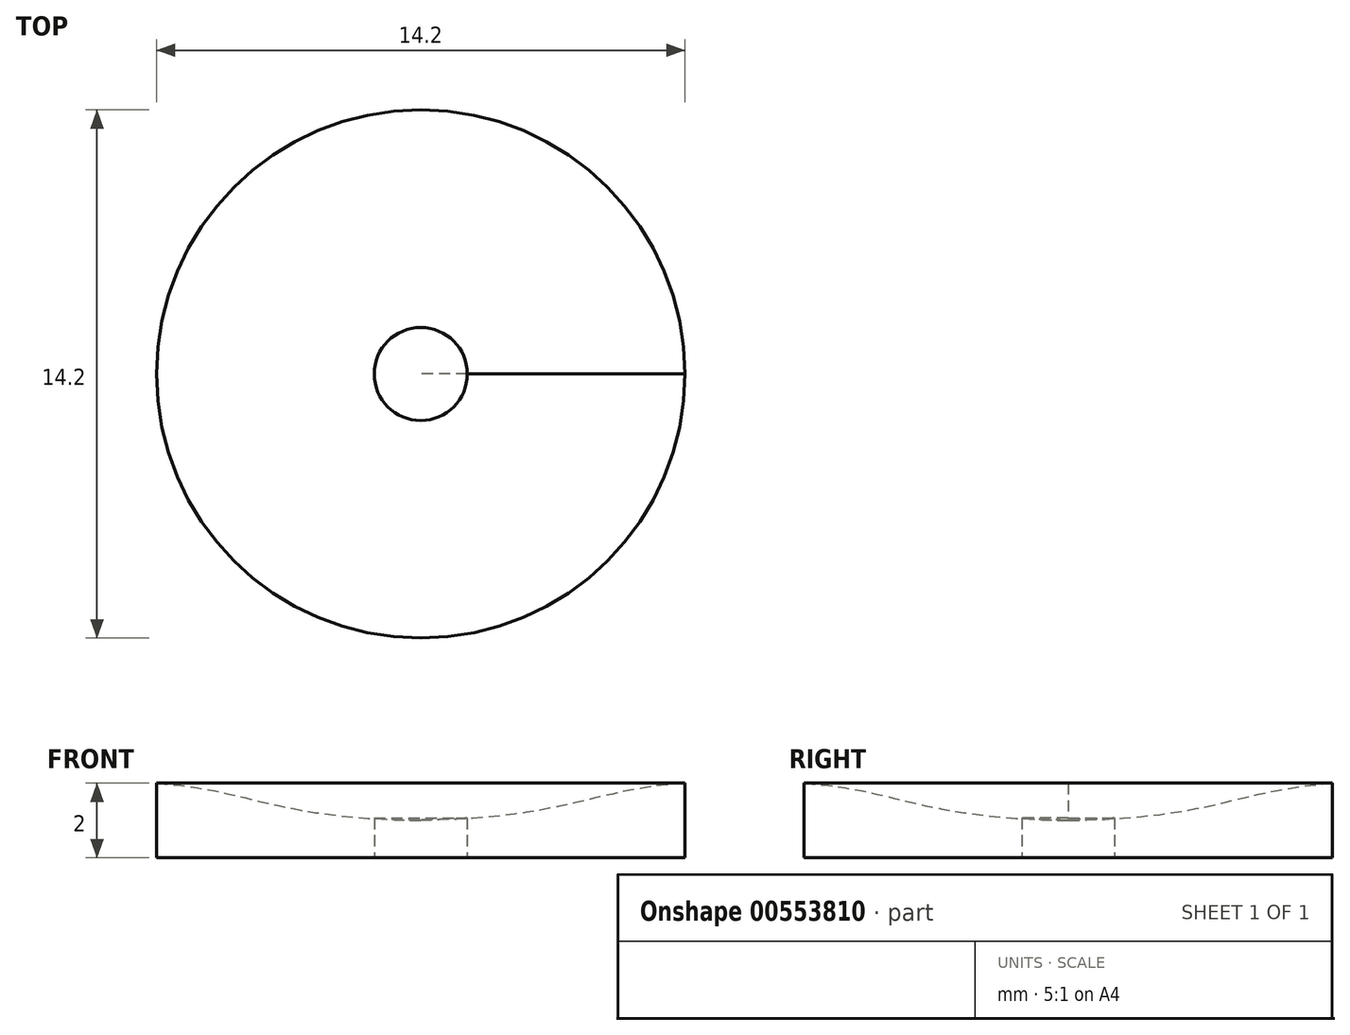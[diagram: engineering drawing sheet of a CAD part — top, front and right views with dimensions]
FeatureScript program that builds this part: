
annotation { "Feature Type Name" : "Feature", "Feature Type Description" : "" }
export const myFeature = defineFeature(function(context is Context, id is Id, definition is map)
    precondition{}
    {
        {
            var Q0;
            Q0=qCreatedBy(makeId("Front.planeOp"),FACE);
            var sketch = newSketch(context, id + "F0", { "sketchPlane" : qUnion([Q0])});
            skLineSegment(sketch, "E0", {"start": v(0, 0) * mm, "end": v(7.1, 0) * mm});
            skLineSegment(sketch, "E1", {"start": v(7.1, 0) * mm, "end": v(7.1, 2) * mm});
            skLineSegment(sketch, "E2", {"start": v(0, 1) * mm, "end": v(0, 0) * mm});
            skFitSpline(sketch, "E3", {"points": [v(7.1, 2) * mm, v(0, 1) * mm], "startDerivative": vector(-7.89, -0.57) * mm, "endDerivative": vector(-12, -0.18) * mm});
            skPoint(sketch, "E4.orphan", {"position": v(0, 2) * mm});
            skSolve(sketch);
        }
        {
            var Q0;
            Q0=makeQuery(id+"F0.imprint","IMPRINT",FACE,{"disambiguationData":[TD([[makeQuery(id+"F0.imprint","IMPRINT",EDGE,{"derivedFrom":sQuery(id+"F0.wireOp",EDGE,"E0")}),1.0]])]});
            var Q1;
            Q1=sQuery(id+"F0.wireOp",EDGE,"E2");
            revolve(context, id + "F1", {"entities" : qUnion([Q0]), "axis" : qUnion([Q1]), "revolveType" : RevolveType.FULL});
        }
        {
            var Q0;
            Q0=makeQuery(id+"F1.opRevolve","SWEPT_FACE",FACE,{"disambiguationData":[OSD([sQuery(id+"F0.wireOp",EDGE,"E0")])]});
            var sketch = newSketch(context, id + "F2", { "sketchPlane" : qUnion([Q0])});
            skPoint(sketch, "E5.middle", {"position": v(0, 0) * mm});
            skCircle(sketch, "E6", {"center": v(0, 0) * mm, "radius": 1.25 * mm});
            skSolve(sketch);
        }
        {
            var Q0;
            Q0=makeQuery(id+"F2.imprint","IMPRINT",FACE,{"disambiguationData":[TD([[makeQuery(id+"F2.imprint","IMPRINT",EDGE,{"derivedFrom":sQuery(id+"F2.wireOp",EDGE,"E5.bottom")}),-1.0]])]});
            var Q1;
            Q1=makeQuery(id+"F2.imprint","IMPRINT",FACE,{"disambiguationData":[TD([[makeQuery(id+"F2.imprint","IMPRINT",EDGE,{"derivedFrom":sQuery(id+"F2.wireOp",EDGE,"E6")}),1.0]])]});
            extrude(context, id + "F3", {"entities" : qUnion([Q0, Q1]), "endBound" : BoundingType.UP_TO_NEXT, "oppositeDirection" : true, "depth" : 25 * mm, "hasOffset" : true, "offsetDistance" : 0.02 * mm, "offsetOppositeDirection" : true});
        }
    });
